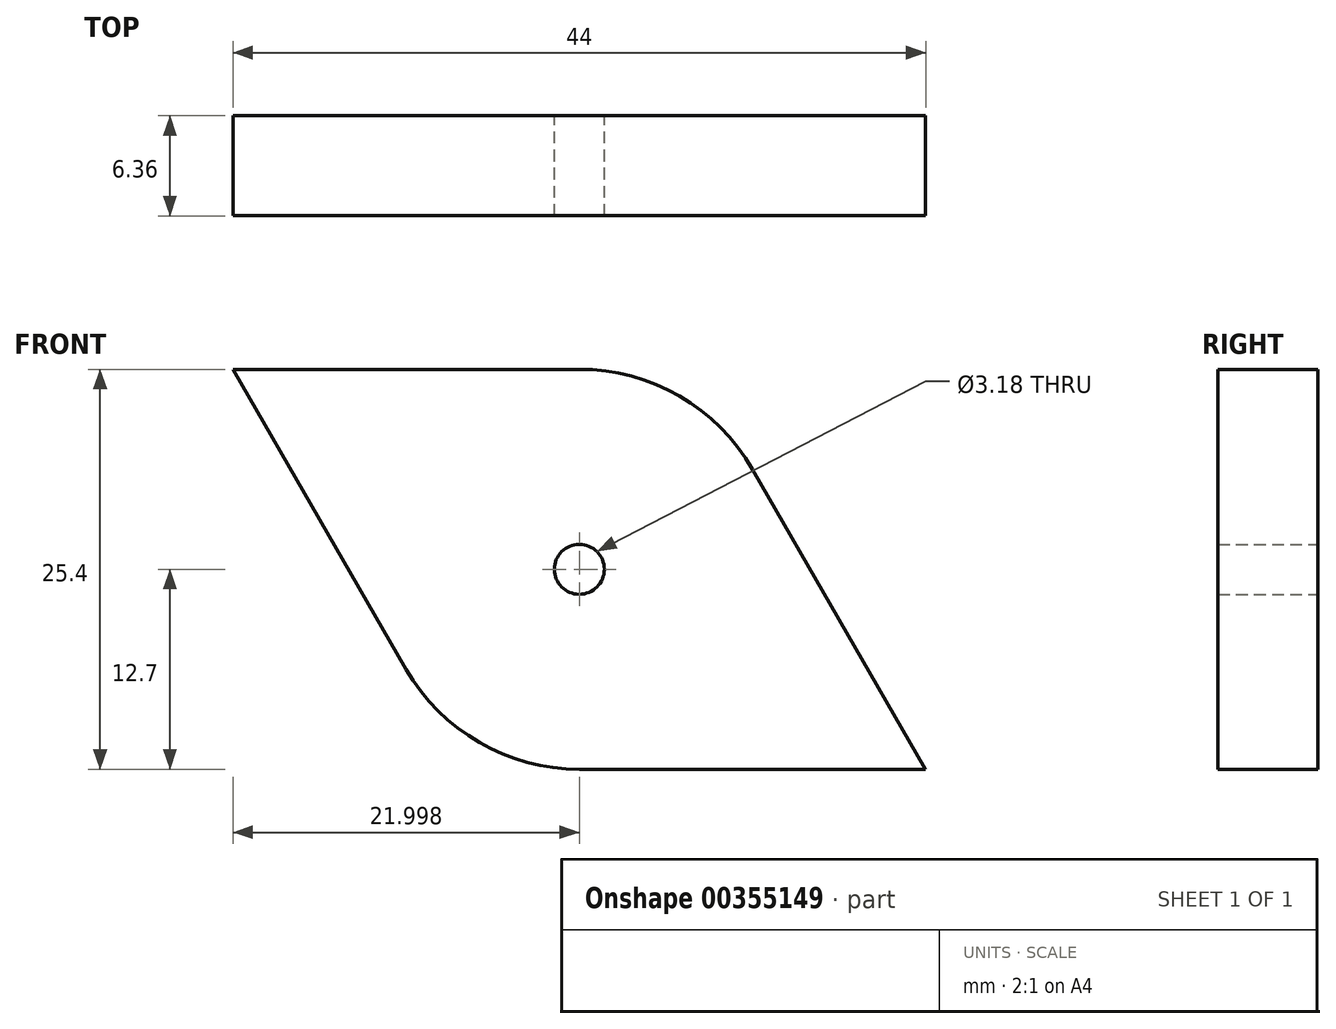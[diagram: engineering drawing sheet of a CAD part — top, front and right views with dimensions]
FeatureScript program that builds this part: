
annotation { "Feature Type Name" : "Feature", "Feature Type Description" : "" }
export const myFeature = defineFeature(function(context is Context, id is Id, definition is map)
    precondition{}
    {
        {
            var Q0;
            Q0=qCreatedBy(makeId("Front.planeOp"),FACE);
            var sketch = newSketch(context, id + "F0", { "sketchPlane" : qUnion([Q0])});
            skLineSegment(sketch, "E0", {"start": v(87.99, -152.4) * mm, "end": v(-263.96, -152.4) * mm});
            skLineSegment(sketch, "E1", {"start": v(-263.96, -152.4) * mm, "end": v(0, 0) * mm});
            skLineSegment(sketch, "E2", {"start": v(0, 0) * mm, "end": v(87.99, -152.4) * mm});
            skLineSegment(sketch, "E3", {"start": v(0, 0) * mm, "end": v(152.4, 87.99) * mm, "construction": true});
            skLineSegment(sketch, "E4", {"start": v(152.4, 87.99) * mm, "end": v(87.99, -152.4) * mm, "construction": true});
            skCircle(sketch, "E5", {"center": v(0, 0) * mm, "radius": 9.53 * mm});
            skCircle(sketch, "E6", {"center": v(0, 0) * mm, "radius": 12.7 * mm});
            skCircle(sketch, "E7", {"center": v(-263.96, -152.4) * mm, "radius": 12.7 * mm});
            skCircle(sketch, "E8", {"center": v(87.99, -152.4) * mm, "radius": 12.7 * mm});
            skLineSegment(sketch, "E9", {"start": v(-6.35, 11) * mm, "end": v(-270.31, -141.4) * mm});
            skLineSegment(sketch, "E10", {"start": v(-263.96, -165.1) * mm, "end": v(87.99, -165.1) * mm});
            skLineSegment(sketch, "E11", {"start": v(98.99, -146.05) * mm, "end": v(11, 6.35) * mm});
            skLineSegment(sketch, "E12", {"start": v(76.99, -158.75) * mm, "end": v(-11, -6.35) * mm});
            skLineSegment(sketch, "E13", {"start": v(-257.61, -163.4) * mm, "end": v(6.35, -11) * mm});
            skLineSegment(sketch, "E14", {"start": v(87.99, -139.7) * mm, "end": v(-263.96, -139.7) * mm});
            skLineSegment(sketch, "E15", {"start": v(87.99, -165.1) * mm, "end": v(109.99, -165.1) * mm});
            skLineSegment(sketch, "E16", {"start": v(98.99, -146.05) * mm, "end": v(109.99, -165.1) * mm});
            skCircle(sketch, "E17", {"center": v(87.99, -152.4) * mm, "radius": 1.59 * mm});
            skCircle(sketch, "E18", {"center": v(-263.96, -152.4) * mm, "radius": 1.59 * mm});
            skLineSegment(sketch, "E19", {"start": v(-270.31, -141.4) * mm, "end": v(-311.36, -165.1) * mm});
            skLineSegment(sketch, "E20", {"start": v(-263.96, -165.1) * mm, "end": v(-311.36, -165.1) * mm});
            skLineSegment(sketch, "E21", {"start": v(-77.11, -139.7) * mm, "end": v(-89.81, -152.4) * mm});
            skLineSegment(sketch, "E22", {"start": v(-89.81, -152.4) * mm, "end": v(-77.11, -165.1) * mm});
            skLineSegment(sketch, "E23", {"start": v(-77.11, -139.7) * mm, "end": v(-77.11, -165.1) * mm});
            skLineSegment(sketch, "E24", {"start": v(-158.96, -139.7) * mm, "end": v(-171.66, -152.4) * mm});
            skLineSegment(sketch, "E25", {"start": v(-171.66, -152.4) * mm, "end": v(-158.96, -165.1) * mm});
            skLineSegment(sketch, "E26", {"start": v(-158.96, -139.7) * mm, "end": v(-158.96, -165.1) * mm});
            skSolve(sketch);
        }
        {
            var Q0;
            {var subQ0=sQuery(id+"F0.wireOp",EDGE,"E17");var subQ1=sQuery(id+"F0.wireOp",EDGE,"E0");var subQ2=makeQuery(id+"F0.imprint","INTERSECT",VERTEX,{"derivedFrom":[subQ1,subQ0]});Q0=makeQuery(id+"F0.imprint","IMPRINT",FACE,{"disambiguationData":[TD([[makeQuery(id+"F0.imprint","IMPRINT",EDGE,{"disambiguationData":[TD([[subQ2,-1.0]])],"derivedFrom":subQ1}),-1.0]])]});}
            var Q1;
            {var subQ5=sQuery(id+"F0.wireOp",EDGE,"E17");var subQ7=sQuery(id+"F0.wireOp",EDGE,"E0");var subQ8=makeQuery(id+"F0.imprint","INTERSECT",VERTEX,{"derivedFrom":[subQ7,subQ5]});Q1=makeQuery(id+"F0.imprint","IMPRINT",FACE,{"disambiguationData":[TD([[makeQuery(id+"F0.imprint","IMPRINT",EDGE,{"disambiguationData":[TD([[subQ8,-1.0]])],"derivedFrom":subQ7}),1.0]])]});}
            var Q2;
            {var subQ0=sQuery(id+"F0.wireOp",EDGE,"E14");var subQ1=sQuery(id+"F0.wireOp",EDGE,"E2");var subQ2=makeQuery(id+"F0.imprint","INTERSECT",VERTEX,{"derivedFrom":[subQ1,subQ0]});Q2=makeQuery(id+"F0.imprint","IMPRINT",FACE,{"disambiguationData":[TD([[makeQuery(id+"F0.imprint","IMPRINT",EDGE,{"disambiguationData":[TD([[subQ2,-1.0]])],"derivedFrom":subQ1}),1.0]])]});}
            var Q3;
            {var subQ3=sQuery(id+"F0.wireOp",EDGE,"E8");var subQ6=sQuery(id+"F0.wireOp",EDGE,"E0");var subQ9=makeQuery(id+"F0.imprint","INTERSECT",VERTEX,{"derivedFrom":[subQ6,subQ3]});Q3=makeQuery(id+"F0.imprint","IMPRINT",FACE,{"disambiguationData":[TD([[makeQuery(id+"F0.imprint","IMPRINT",EDGE,{"disambiguationData":[TD([[subQ9,-1.0]])],"derivedFrom":subQ6}),-1.0]])]});}
            var Q4;
            {var subQ0=sQuery(id+"F0.wireOp",EDGE,"E8");var subQ1=sQuery(id+"F0.wireOp",EDGE,"E0");var subQ2=makeQuery(id+"F0.imprint","INTERSECT",VERTEX,{"derivedFrom":[subQ1,subQ0]});Q4=makeQuery(id+"F0.imprint","IMPRINT",FACE,{"disambiguationData":[TD([[makeQuery(id+"F0.imprint","IMPRINT",EDGE,{"disambiguationData":[TD([[subQ2,-1.0]])],"derivedFrom":subQ1}),1.0]])]});}
            var Q5;
            {var subQ0=sQuery(id+"F0.wireOp",EDGE,"E15");Q5=makeQuery(id+"F0.imprint","IMPRINT",FACE,{"disambiguationData":[TD([[makeQuery(id+"F0.imprint","IMPRINT",EDGE,{"derivedFrom":subQ0}),1.0]])]});}
            extrude(context, id + "F1", {"entities" : qUnion([Q0, Q1, Q2, Q3, Q4, Q5]), "endBound" : BoundingType.SYMMETRIC, "depth" : 6.35 * mm});
        }
    });
